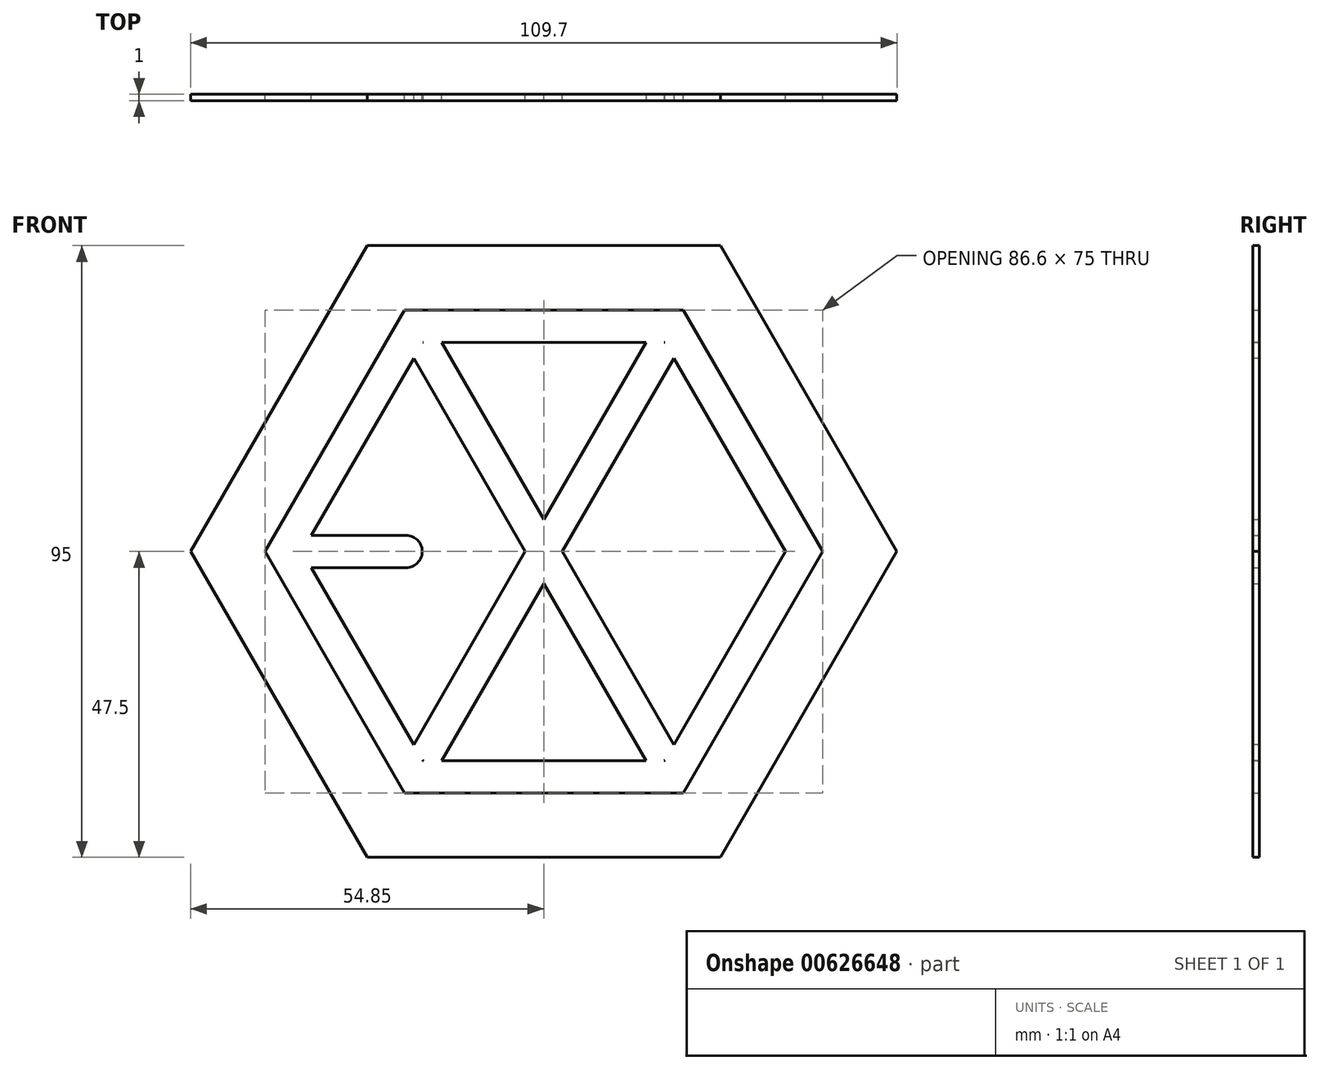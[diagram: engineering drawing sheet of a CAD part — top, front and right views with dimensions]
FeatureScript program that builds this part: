
annotation { "Feature Type Name" : "Feature", "Feature Type Description" : "" }
export const myFeature = defineFeature(function(context is Context, id is Id, definition is map)
    precondition{}
    {
        {
            var Q0;
            Q0=qCreatedBy(makeId("Front.planeOp"),FACE);
            var sketch = newSketch(context, id + "F0", { "sketchPlane" : qUnion([Q0])});
            skCircle(sketch, "E0.cCircle", {"center": v(0, 0) * mm, "radius": 47.5 * mm, "construction": true});
            skLineSegment(sketch, "E0.0", {"start": v(27.42, -47.5) * mm, "end": v(-27.42, -47.5) * mm});
            skLineSegment(sketch, "E0.1", {"start": v(-27.42, -47.5) * mm, "end": v(-54.85, 0) * mm});
            skLineSegment(sketch, "E0.2", {"start": v(-54.85, 0) * mm, "end": v(-27.42, 47.5) * mm});
            skLineSegment(sketch, "E0.3", {"start": v(-27.42, 47.5) * mm, "end": v(27.42, 47.5) * mm});
            skLineSegment(sketch, "E0.4", {"start": v(27.42, 47.5) * mm, "end": v(54.85, 0) * mm});
            skLineSegment(sketch, "E0.5", {"start": v(54.85, 0) * mm, "end": v(27.42, -47.5) * mm});
            skPoint(sketch, "E0.0.midPoint", {"position": v(0, -47.5) * mm});
            skCircle(sketch, "E1.cCircle", {"center": v(0, 0) * mm, "radius": 37.5 * mm, "construction": true});
            skLineSegment(sketch, "E1.0", {"start": v(43.3, 0) * mm, "end": v(21.65, -37.5) * mm});
            skLineSegment(sketch, "E1.1", {"start": v(21.65, -37.5) * mm, "end": v(-21.65, -37.5) * mm});
            skLineSegment(sketch, "E1.2", {"start": v(-21.65, -37.5) * mm, "end": v(-43.3, 0) * mm});
            skLineSegment(sketch, "E1.3", {"start": v(-43.3, 0) * mm, "end": v(-21.65, 37.5) * mm});
            skLineSegment(sketch, "E1.4", {"start": v(-21.65, 37.5) * mm, "end": v(21.65, 37.5) * mm});
            skLineSegment(sketch, "E1.5", {"start": v(21.65, 37.5) * mm, "end": v(43.3, 0) * mm});
            skPoint(sketch, "E1.0.midPoint", {"position": v(32.48, -18.75) * mm});
            skSolve(sketch);
        }
        {
            var Q0;
            Q0=qCreatedBy(makeId("Front.planeOp"),FACE);
            var sketch = newSketch(context, id + "F1", { "sketchPlane" : qUnion([Q0])});
            skLineSegment(sketch, "E2.bottom", {"start": v(-20.92, -31.23) * mm, "end": v(16.58, 33.73) * mm});
            skLineSegment(sketch, "E2.top", {"start": v(-16.58, -33.73) * mm, "end": v(20.92, 31.23) * mm});
            skLineSegment(sketch, "E2.left", {"start": v(-20.92, -31.23) * mm, "end": v(-16.58, -33.73) * mm});
            skLineSegment(sketch, "E2.right", {"start": v(16.58, 33.73) * mm, "end": v(20.92, 31.23) * mm});
            skPoint(sketch, "E2.middle", {"position": v(0, 0) * mm});
            skSolve(sketch);
        }
        {
            var Q0;
            Q0=qCreatedBy(makeId("Front.planeOp"),FACE);
            var sketch = newSketch(context, id + "F2", { "sketchPlane" : qUnion([Q0])});
            skLineSegment(sketch, "E3.bottom", {"start": v(-16.58, 33.73) * mm, "end": v(20.92, -31.23) * mm});
            skLineSegment(sketch, "E3.top", {"start": v(-20.92, 31.23) * mm, "end": v(16.58, -33.73) * mm});
            skLineSegment(sketch, "E3.left", {"start": v(-16.58, 33.73) * mm, "end": v(-20.92, 31.23) * mm});
            skLineSegment(sketch, "E3.right", {"start": v(20.92, -31.23) * mm, "end": v(16.58, -33.73) * mm});
            skPoint(sketch, "E3.middle", {"position": v(0, 0) * mm});
            skSolve(sketch);
        }
        {
            var Q0;
            Q0=qCreatedBy(makeId("Front.planeOp"),FACE);
            var sketch = newSketch(context, id + "F3", { "sketchPlane" : qUnion([Q0])});
            skCircle(sketch, "E4.cCircle", {"center": v(0, 0) * mm, "radius": 32.5 * mm, "construction": true});
            skLineSegment(sketch, "E4.0", {"start": v(18.76, -32.5) * mm, "end": v(-18.76, -32.5) * mm});
            skLineSegment(sketch, "E4.1", {"start": v(-18.76, -32.5) * mm, "end": v(-37.53, 0) * mm});
            skLineSegment(sketch, "E4.2", {"start": v(-37.53, 0) * mm, "end": v(-18.76, 32.5) * mm});
            skLineSegment(sketch, "E4.3", {"start": v(-18.76, 32.5) * mm, "end": v(18.76, 32.5) * mm});
            skLineSegment(sketch, "E4.4", {"start": v(18.76, 32.5) * mm, "end": v(37.53, 0) * mm});
            skLineSegment(sketch, "E4.5", {"start": v(37.53, 0) * mm, "end": v(18.76, -32.5) * mm});
            skPoint(sketch, "E4.0.midPoint", {"position": v(0, -32.5) * mm});
            skSolve(sketch);
        }
        {
            var Q0;
            Q0=qCreatedBy(makeId("Front.planeOp"),FACE);
            var sketch = newSketch(context, id + "F4", { "sketchPlane" : qUnion([Q0])});
            skLineSegment(sketch, "E5.bottom", {"start": v(-41.38, 2.5) * mm, "end": v(-21.38, 2.5) * mm});
            skLineSegment(sketch, "E5.top", {"start": v(-41.38, -2.5) * mm, "end": v(-21.38, -2.5) * mm});
            skLineSegment(sketch, "E5.left", {"start": v(-41.38, 2.5) * mm, "end": v(-41.38, -2.5) * mm});
            skLineSegment(sketch, "E5.right", {"start": v(-21.38, 2.5) * mm, "end": v(-21.38, -2.5) * mm});
            skPoint(sketch, "E5.middle", {"position": v(-31.38, 0) * mm});
            skSolve(sketch);
        }
        {
            var Q0;
            Q0=qCreatedBy(makeId("Front.planeOp"),FACE);
            var sketch = newSketch(context, id + "F5", { "sketchPlane" : qUnion([Q0])});
            skCircle(sketch, "E6", {"center": v(-21.38, 0) * mm, "radius": 2.5 * mm});
            skSolve(sketch);
        }
        {
            var Q0;
            Q0 = qSketchRegion(id + "F0", true);
            extrude(context, id + "F6", {"entities" : qUnion([Q0]), "depth" : 1 * mm, "offsetDistance" : 25 * mm});
        }
        {
            var Q0;
            Q0 = qSketchRegion(id + "F3", true);
            extrude(context, id + "F7", {"entities" : qUnion([Q0]), "depth" : 1 * mm, "offsetDistance" : 25 * mm});
        }
        {
            var Q0;
            Q0 = qSketchRegion(id + "F1", true);
            var Q1;
            Q1 = qSketchRegion(id + "F2", true);
            var Q2;
            Q2 = qSketchRegion(id + "F4", true);
            var Q3;
            Q3 = qSketchRegion(id + "F5", true);
            extrude(context, id + "F8", {"entities" : qUnion([Q0, Q1, Q2, Q3]), "operationType" : NewBodyOperationType.REMOVE, "depth" : 1 * mm, "offsetDistance" : 25 * mm});
        }
    });
